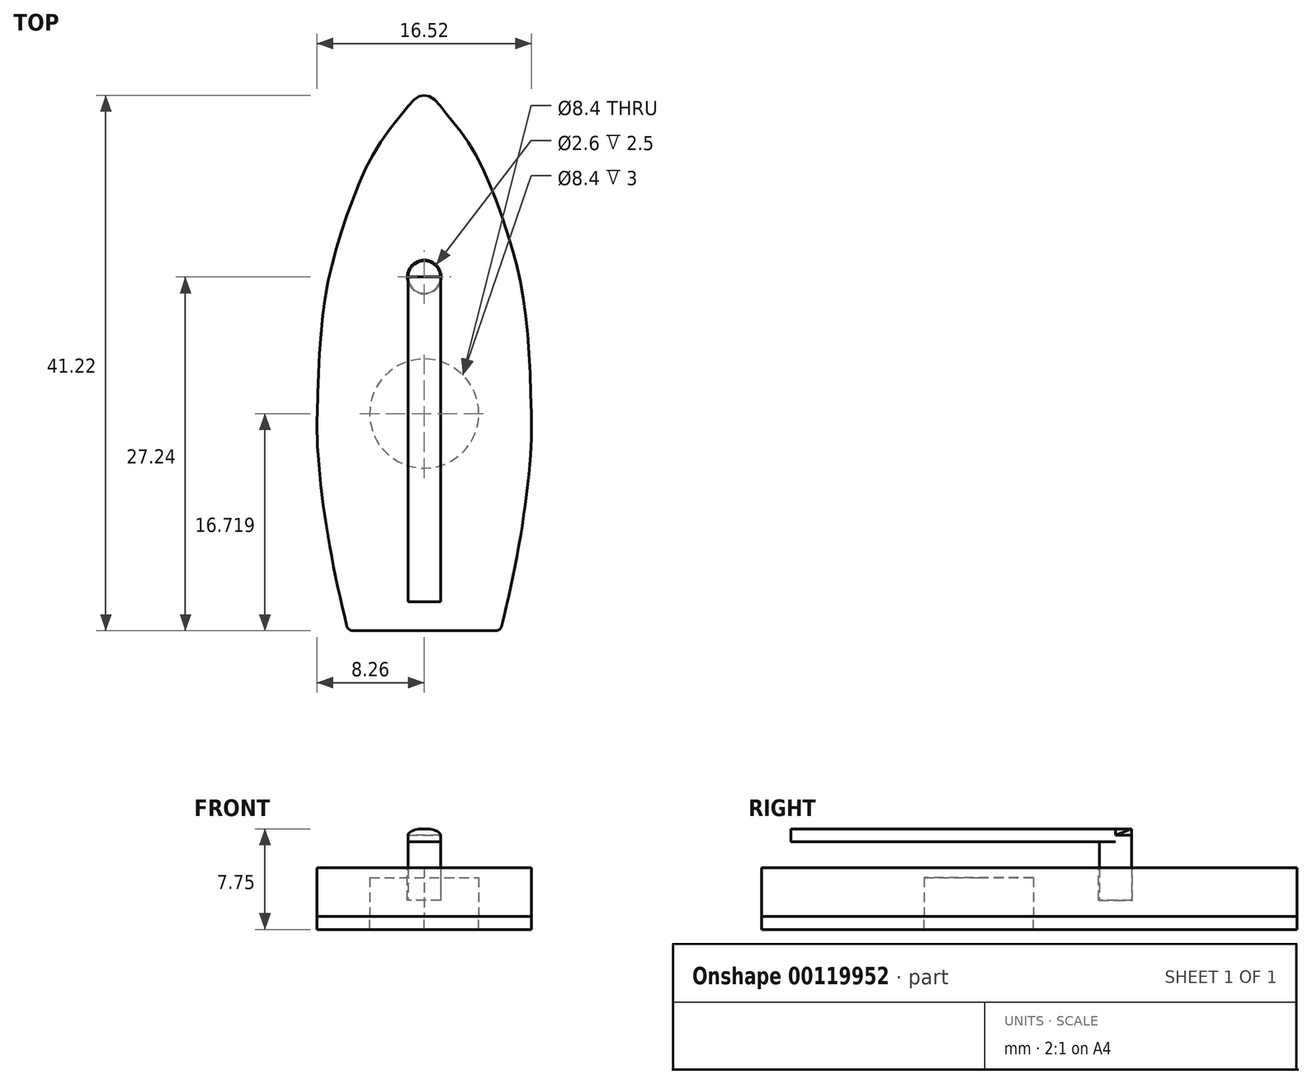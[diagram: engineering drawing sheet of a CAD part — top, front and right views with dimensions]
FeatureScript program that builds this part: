
annotation { "Feature Type Name" : "Feature", "Feature Type Description" : "" }
export const myFeature = defineFeature(function(context is Context, id is Id, definition is map)
    precondition{}
    {
        {
            var Q0;
            Q0=qCreatedBy(makeId("Top.planeOp"),FACE);
            var sketch = newSketch(context, id + "F0", { "sketchPlane" : qUnion([Q0])});
            skPoint(sketch, "E0", {"position": v(-9.86, 46.47) * mm});
            skPoint(sketch, "E1", {"position": v(-9.86, 4.47) * mm});
            skLineSegment(sketch, "E2", {"start": v(-9.86, 46.47) * mm, "end": v(-9.86, 4.47) * mm, "construction": true});
            skPoint(sketch, "E3", {"position": v(-18.1, 21.97) * mm});
            skPoint(sketch, "E4", {"position": v(-1.6, 21.97) * mm});
            skLineSegment(sketch, "E5", {"start": v(-18.1, 21.97) * mm, "end": v(-1.6, 21.97) * mm, "construction": true});
            skPoint(sketch, "E6", {"position": v(-4, 5.25) * mm});
            skPoint(sketch, "E7", {"position": v(-15.74, 5.25) * mm});
            skFitSpline(sketch, "E8", {"points": [v(-18.1, 21.97) * mm, v(-17.56, 30.4) * mm, v(-16.01, 36.64) * mm, v(-13.6, 42.27) * mm, v(-11.6, 45.02) * mm, v(-10.42, 46.32) * mm, v(-9.86, 46.47) * mm], "startDerivative": vector(1.06, 35.84) * mm, "endDerivative": vector(8.44, 0.76) * mm});
            skFitSpline(sketch, "E9.MirrorCS", {"points": [v(-1.62, 21.97) * mm, v(-2.16, 30.4) * mm, v(-3.7, 36.64) * mm, v(-6.12, 42.27) * mm, v(-8.13, 45.02) * mm, v(-9.3, 46.32) * mm, v(-9.86, 46.47) * mm], "startDerivative": vector(-1.06, 35.84) * mm, "endDerivative": vector(-8.44, 0.76) * mm});
            skFitSpline(sketch, "E10", {"points": [v(-18.1, 21.97) * mm, v(-18.1, 20.01) * mm, v(-17.71, 15.57) * mm, v(-16.85, 10.22) * mm, v(-15.74, 5.25) * mm], "startDerivative": vector(-0.25, -10.19) * mm, "endDerivative": vector(4.13, -17.64) * mm});
            skLineSegment(sketch, "E11", {"start": v(-15.74, 5.25) * mm, "end": v(-9.86, 5.25) * mm});
            skLineSegment(sketch, "E12.MirrorCS", {"start": v(-3.98, 5.25) * mm, "end": v(-9.86, 5.25) * mm});
            skFitSpline(sketch, "E13.MirrorCS", {"points": [v(-1.62, 21.97) * mm, v(-1.62, 20.01) * mm, v(-2, 15.57) * mm, v(-2.87, 10.22) * mm, v(-3.98, 5.25) * mm], "startDerivative": vector(0.25, -10.19) * mm, "endDerivative": vector(-4.13, -17.64) * mm});
            skPoint(sketch, "E14", {"position": v(-9.86, 32.5) * mm});
            skCircle(sketch, "E15", {"center": v(-9.86, 32.5) * mm, "radius": 1.25 * mm});
            skSolve(sketch);
        }
        {
            var Q0;
            Q0=makeQuery(id+"F0.imprint","IMPRINT",FACE,{"disambiguationData":[TD([[makeQuery(id+"F0.imprint","IMPRINT",EDGE,{"derivedFrom":sQuery(id+"F0.wireOp",EDGE,"E8")}),-1.0]])]});
            extrude(context, id + "F1", {"entities" : qUnion([Q0]), "depth" : (7.5 / 2) * mm});
        }
        {
            var Q0;
            Q0=makeQuery(id+"F1.opExtrude","SWEPT_EDGE",EDGE,{"disambiguationData":[OSD([sQuery(id+"F0.wireOp",EDGE,"E12.MirrorCS"),sQuery(id+"F0.wireOp",EDGE,"E13.MirrorCS")])]});
            var Q1;
            Q1=makeQuery(id+"F1.opExtrude","SWEPT_EDGE",EDGE,{"disambiguationData":[OSD([sQuery(id+"F0.wireOp",EDGE,"E10"),sQuery(id+"F0.wireOp",EDGE,"E11")])]});
            fillet(context, id + "F2", {"entities" : qUnion([Q0, Q1]), "radius" : 0.5 * mm, "tangentPropagation" : true, "allowEdgeOverflow" : false});
        }
        {
            var Q0;
            Q0=makeQuery(id+"F0.imprint","IMPRINT",FACE,{"disambiguationData":[TD([[makeQuery(id+"F0.imprint","IMPRINT",EDGE,{"derivedFrom":sQuery(id+"F0.wireOp",EDGE,"E15")}),1.0]])]});
            extrude(context, id + "F3", {"entities" : qUnion([Q0]), "operationType" : NewBodyOperationType.ADD, "depth" : 1.25 * mm});
        }
        {
            var Q0;
            {var subQ0=sQuery(id+"F0.wireOp",EDGE,"E15");Q0=makeQuery(id+"F3.boolean.opBoolean","MERGE",FACE,{"derivedFrom":[makeQuery(id+"F1.opExtrude","CAP_FACE",FACE,{"disambiguationData":[OSD([sQuery(id+"F0.wireOp",EDGE,"E8"),sQuery(id+"F0.wireOp",EDGE,"E9.MirrorCS"),sQuery(id+"F0.wireOp",EDGE,"E10"),sQuery(id+"F0.wireOp",EDGE,"E11"),sQuery(id+"F0.wireOp",EDGE,"E12.MirrorCS"),sQuery(id+"F0.wireOp",EDGE,"E13.MirrorCS"),subQ0])],"isStart":true}),makeQuery(id+"F3.opExtrude","CAP_FACE",FACE,{"disambiguationData":[OSD([subQ0])],"isStart":true})]});}
            var sketch = newSketch(context, id + "F4", { "sketchPlane" : qUnion([Q0])});
            skLineSegment(sketch, "E16", {"start": v(-1.62, -21.97) * mm, "end": v(-18.1, -21.97) * mm, "construction": true});
            skCircle(sketch, "E17", {"center": v(-9.86, -21.97) * mm, "radius": 4 * mm});
            skSolve(sketch);
        }
        {
            var Q0;
            Q0=makeQuery(id+"F4.imprint","IMPRINT",FACE,{"disambiguationData":[TD([[makeQuery(id+"F4.imprint","IMPRINT",EDGE,{"derivedFrom":sQuery(id+"F4.wireOp",EDGE,"E17")}),-1.0]])]});
            var Q1;
            Q1=makeQuery(id+"F4.imprint","IMPRINT",FACE,{"disambiguationData":[TD([[makeQuery(id+"F4.imprint","IMPRINT",EDGE,{"derivedFrom":sQuery(id+"F4.wireOp",EDGE,"E17")}),1.0]])]});
            extrude(context, id + "F5", {"entities" : qUnion([Q0, Q1]), "depth" : 1 * mm});
        }
        {
            var Q0;
            Q0 = qSketchRegion(id + "F4", true);
            extrude(context, id + "F6", {"entities" : qUnion([Q0]), "operationType" : NewBodyOperationType.REMOVE, "oppositeDirection" : true, "depth" : 3 * mm});
        }
        {
            var Q0;
            Q0=makeQuery(id+"F3.opExtrude","CAP_FACE",FACE,{"disambiguationData":[OSD([sQuery(id+"F0.wireOp",EDGE,"E15")])],"isStart":false});
            extrude(context, id + "F7", {"entities" : qUnion([Q0]), "depth" : 5 * mm});
        }
        {
            var Q0;
            Q0=makeQuery(id+"F7.opExtrude","CAP_FACE",FACE,{"disambiguationData":[OSD([sQuery(id+"F0.wireOp",EDGE,"E15")])],"isStart":false});
            var sketch = newSketch(context, id + "F8", { "sketchPlane" : qUnion([Q0])});
            skPoint(sketch, "E18", {"position": v(-9.86, 32.5) * mm});
            skLineSegment(sketch, "E19", {"start": v(-11.1, 32.5) * mm, "end": v(-8.6, 32.5) * mm});
            skSolve(sketch);
        }
        {
            var Q0;
            Q0=sQuery(id+"F8.wireOp",EDGE,"E19");
            var Q1;
            Q1=makeQuery(id+"F7.opExtrude","CAP_EDGE",EDGE,{"disambiguationData":[OSD([sQuery(id+"F0.wireOp",EDGE,"E15")])],"isStart":false});
            cPlane(context, id + "F9", {"entities" : qUnion([Q0, Q1]), "cplaneType" : CPlaneType.LINE_ANGLE, "offset" : 25 * mm, "angle" : 0 * degree, "width" : 150 * mm, "height" : 150 * mm});
        }
        {
            var Q0;
            Q0=qCreatedBy(id+"F9.planeOp",FACE);
            var sketch = newSketch(context, id + "F10", { "sketchPlane" : qUnion([Q0])});
            skLineSegment(sketch, "E20.0", {"start": v(-11.1, 6.25) * mm, "end": v(-8.6, 6.25) * mm});
            skLineSegment(sketch, "E21", {"start": v(-11.1, 4.75) * mm, "end": v(-11.1, 5.75) * mm});
            skLineSegment(sketch, "E22", {"start": v(-8.6, 6.25) * mm, "end": v(-8.6, 5.75) * mm});
            skLineSegment(sketch, "E23", {"start": v(-11.1, 5.75) * mm, "end": v(-8.6, 5.75) * mm});
            skEllipse(sketch, "E24", {"center": v(-9.86, 6.25) * mm, "majorRadius": 1.25 * mm, "minorRadius": 0.5 * mm, "majorAxis": v(-1, 0)});
            skPoint(sketch, "E25", {"position": v(-9.86, 6.75) * mm});
            skLineSegment(sketch, "E26", {"start": v(-11.1, 6.25) * mm, "end": v(-11.1, 5.75) * mm});
            skSolve(sketch);
        }
        {
            var Q0;
            Q0 = qSketchRegion(id + "F10", true);
            extrude(context, id + "F11", {"entities" : qUnion([Q0]), "operationType" : NewBodyOperationType.ADD, "depth" : 25 * mm});
        }
        {
            var Q0;
            {var subQ0=sQuery(id+"F8.wireOp",EDGE,"E19");Q0=makeQuery(id+"F8.imprint","IMPRINT",FACE,{"disambiguationData":[TD([[makeQuery(id+"F8.imprint","IMPRINT",EDGE,{"derivedFrom":subQ0}),1.0]])]});}
            extrude(context, id + "F12", {"entities" : qUnion([Q0]), "depth" : 1 * mm});
        }
        {
            var Q0;
            {var subQ0=sQuery(id+"F10.wireOp",EDGE,"E21");Q0=makeQuery(id+"F10.imprint","IMPRINT",FACE,{"disambiguationData":[TD([[makeQuery(id+"F10.imprint","IMPRINT",EDGE,{"derivedFrom":subQ0}),-1.0]])]});}
            var Q1;
            {var subQ0=sQuery(id+"F10.wireOp",EDGE,"E20.0");Q1=makeQuery(id+"F10.imprint","IMPRINT",FACE,{"disambiguationData":[TD([[makeQuery(id+"F10.imprint","IMPRINT",EDGE,{"derivedFrom":subQ0}),1.0]])]});}
            var Q2;
            {var subQ0=sQuery(id+"F10.wireOp",EDGE,"E20.0");Q2=makeQuery(id+"F10.imprint","IMPRINT",FACE,{"disambiguationData":[TD([[makeQuery(id+"F10.imprint","IMPRINT",EDGE,{"derivedFrom":subQ0}),-1.0]])]});}
            extrude(context, id + "F13", {"entities" : qUnion([Q0, Q1, Q2]), "oppositeDirection" : true, "depth" : 5 * mm});
        }
        {
            var Q0;
            Q0=makeQuery(id+"F13.opExtrude","SWEPT_BODY",BODY,{"disambiguationData":[OSD([sQuery(id+"F10.wireOp",EDGE,"E21"),sQuery(id+"F10.wireOp",EDGE,"E22"),sQuery(id+"F10.wireOp",EDGE,"E23"),sQuery(id+"F10.wireOp",EDGE,"E24")])]});
            var Q1;
            Q1=makeQuery(id+"F12.opExtrude","SWEPT_BODY",BODY,{"disambiguationData":[OSD([sQuery(id+"F0.wireOp",EDGE,"E15"),sQuery(id+"F8.wireOp",EDGE,"E19")])]});
            booleanBodies(context, id + "F14", {"operationType" : BooleanOperationType.INTERSECTION, "tools" : qUnion([Q0, Q1])});
        }
        {
            var Q0;
            Q0=makeQuery(id+"F1.opExtrude","CAP_FACE",FACE,{"disambiguationData":[OSD([sQuery(id+"F0.wireOp",EDGE,"E8"),sQuery(id+"F0.wireOp",EDGE,"E9.MirrorCS"),sQuery(id+"F0.wireOp",EDGE,"E10"),sQuery(id+"F0.wireOp",EDGE,"E11"),sQuery(id+"F0.wireOp",EDGE,"E12.MirrorCS"),sQuery(id+"F0.wireOp",EDGE,"E13.MirrorCS"),sQuery(id+"F0.wireOp",EDGE,"E15")])],"isStart":false});
            var sketch = newSketch(context, id + "F15", { "sketchPlane" : qUnion([Q0])});
            skCircle(sketch, "E27.0", {"center": v(-9.86, 32.5) * mm, "radius": 1.3 * mm});
            skSolve(sketch);
        }
        {
            var Q0;
            Q0=makeQuery(id+"F15.imprint","IMPRINT",FACE,{"disambiguationData":[TD([[makeQuery(id+"F15.imprint","IMPRINT",EDGE,{"derivedFrom":sQuery(id+"F15.wireOp",EDGE,"E27.0")}),1.0]])]});
            var Q1;
            Q1=makeQuery(id+"F3.opExtrude","CAP_FACE",FACE,{"disambiguationData":[OSD([sQuery(id+"F0.wireOp",EDGE,"E15")])],"isStart":false});
            extrude(context, id + "F16", {"entities" : qUnion([Q0]), "operationType" : NewBodyOperationType.REMOVE, "endBound" : BoundingType.UP_TO_SURFACE, "oppositeDirection" : true, "endBoundEntityFace" : qUnion([Q1]), "depth" : 25 * mm});
        }
        {
            var Q0;
            {var subQ0=sQuery(id+"F0.wireOp",EDGE,"E15");Q0=makeQuery(id+"F3.boolean.opBoolean","MERGE",FACE,{"derivedFrom":[makeQuery(id+"F1.opExtrude","CAP_FACE",FACE,{"disambiguationData":[OSD([sQuery(id+"F0.wireOp",EDGE,"E8"),sQuery(id+"F0.wireOp",EDGE,"E9.MirrorCS"),sQuery(id+"F0.wireOp",EDGE,"E10"),sQuery(id+"F0.wireOp",EDGE,"E11"),sQuery(id+"F0.wireOp",EDGE,"E12.MirrorCS"),sQuery(id+"F0.wireOp",EDGE,"E13.MirrorCS"),subQ0])],"isStart":true}),makeQuery(id+"F3.opExtrude","CAP_FACE",FACE,{"disambiguationData":[OSD([subQ0])],"isStart":true})]});}
            var sketch = newSketch(context, id + "F17", { "sketchPlane" : qUnion([Q0])});
            skCircle(sketch, "E28.0", {"center": v(-9.86, -21.97) * mm, "radius": 4.2 * mm});
            skSolve(sketch);
        }
        {
            var Q0;
            Q0=makeQuery(id+"F17.imprint","IMPRINT",FACE,{"disambiguationData":[TD([[makeQuery(id+"F17.imprint","IMPRINT",EDGE,{"derivedFrom":sQuery(id+"F17.wireOp",EDGE,"E28.0")}),1.0]])]});
            var Q1;
            Q1=makeQuery(id+"F6.boolean.opBoolean","COPY",FACE,{"derivedFrom":makeQuery(id+"F6.opExtrude","CAP_FACE",FACE,{"disambiguationData":[OSD([sQuery(id+"F4.wireOp",EDGE,"E17")])],"isStart":false})});
            extrude(context, id + "F18", {"entities" : qUnion([Q0]), "operationType" : NewBodyOperationType.REMOVE, "endBound" : BoundingType.UP_TO_SURFACE, "oppositeDirection" : true, "endBoundEntityFace" : qUnion([Q1]), "depth" : 25 * mm});
        }
        {
            var Q0;
            {var subQ0=sQuery(id+"F0.wireOp",EDGE,"E15");Q0=makeQuery(id+"F3.boolean.opBoolean","MERGE",FACE,{"derivedFrom":[makeQuery(id+"F1.opExtrude","CAP_FACE",FACE,{"disambiguationData":[OSD([sQuery(id+"F0.wireOp",EDGE,"E8"),sQuery(id+"F0.wireOp",EDGE,"E9.MirrorCS"),sQuery(id+"F0.wireOp",EDGE,"E10"),sQuery(id+"F0.wireOp",EDGE,"E11"),sQuery(id+"F0.wireOp",EDGE,"E12.MirrorCS"),sQuery(id+"F0.wireOp",EDGE,"E13.MirrorCS"),subQ0])],"isStart":true}),makeQuery(id+"F3.opExtrude","CAP_FACE",FACE,{"disambiguationData":[OSD([subQ0])],"isStart":true})]});}
            var sketch = newSketch(context, id + "F19", { "sketchPlane" : qUnion([Q0])});
            skCircle(sketch, "E29.0", {"center": v(-9.86, -21.97) * mm, "radius": 4.2 * mm});
            skSolve(sketch);
        }
        {
            var Q0;
            Q0=makeQuery(id+"F19.imprint","IMPRINT",FACE,{"disambiguationData":[TD([[makeQuery(id+"F19.imprint","IMPRINT",EDGE,{"derivedFrom":sQuery(id+"F19.wireOp",EDGE,"E29.0")}),1.0]])]});
            var Q1;
            Q1=makeQuery(id+"F5.opExtrude","CAP_FACE",FACE,{"disambiguationData":[OSD([sQuery(id+"F0.wireOp",EDGE,"E8"),sQuery(id+"F0.wireOp",EDGE,"E9.MirrorCS"),sQuery(id+"F0.wireOp",EDGE,"E10"),sQuery(id+"F0.wireOp",EDGE,"E11"),sQuery(id+"F0.wireOp",EDGE,"E12.MirrorCS"),sQuery(id+"F0.wireOp",EDGE,"E13.MirrorCS"),sQuery(id+"F0.wireOp",EDGE,"E15")])],"isStart":false});
            extrude(context, id + "F20", {"entities" : qUnion([Q0]), "endBound" : BoundingType.UP_TO_SURFACE, "endBoundEntityFace" : qUnion([Q1]), "depth" : 25 * mm});
        }
        {
            var Q0;
            Q0=makeQuery(id+"F20.opExtrude","SWEPT_BODY",BODY,{"disambiguationData":[OSD([sQuery(id+"F19.wireOp",EDGE,"E29.0")])]});
            var Q1;
            Q1=makeQuery(id+"F5.opExtrude","SWEPT_BODY",BODY,{"disambiguationData":[OSD([sQuery(id+"F0.wireOp",EDGE,"E8"),sQuery(id+"F0.wireOp",EDGE,"E9.MirrorCS"),sQuery(id+"F0.wireOp",EDGE,"E10"),sQuery(id+"F0.wireOp",EDGE,"E11"),sQuery(id+"F0.wireOp",EDGE,"E12.MirrorCS"),sQuery(id+"F0.wireOp",EDGE,"E13.MirrorCS"),sQuery(id+"F0.wireOp",EDGE,"E15")])]});
            booleanBodies(context, id + "F21", {"operationType" : BooleanOperationType.SUBTRACTION, "tools" : qUnion([Q0]), "targets" : qUnion([Q1]), "keepTools" : true});
        }
    });
